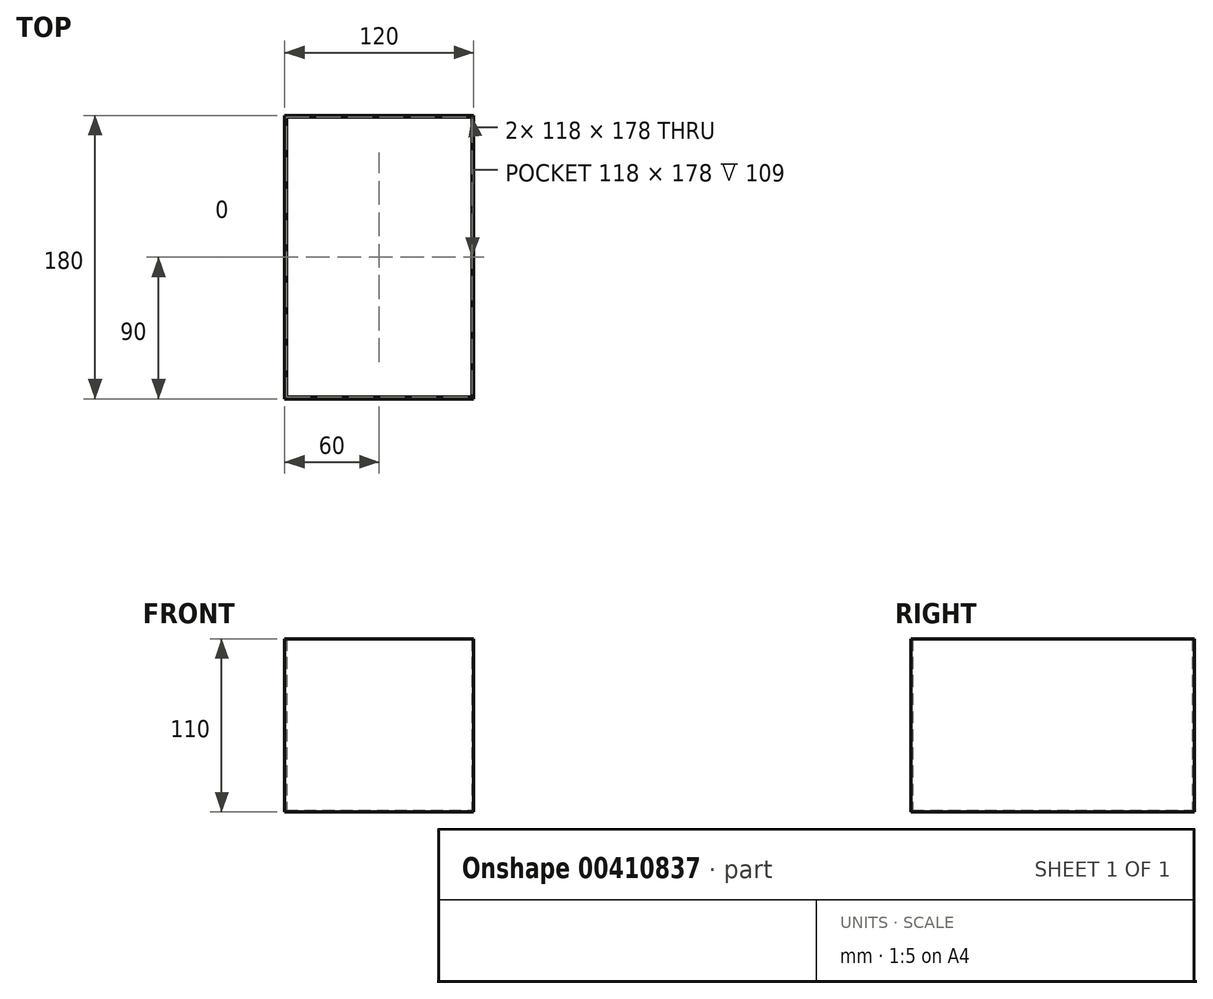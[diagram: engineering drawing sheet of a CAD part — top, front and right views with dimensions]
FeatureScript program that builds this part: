
annotation { "Feature Type Name" : "Feature", "Feature Type Description" : "" }
export const myFeature = defineFeature(function(context is Context, id is Id, definition is map)
    precondition{}
    {
        {
            var Q0;
            Q0=qCreatedBy(makeId("Top.planeOp"),FACE);
            var sketch = newSketch(context, id + "F0", { "sketchPlane" : qUnion([Q0])});
            skLineSegment(sketch, "E0.bottom", {"start": v(0, 0) * mm, "end": v(120, 0) * mm});
            skLineSegment(sketch, "E0.left", {"start": v(0, 0) * mm, "end": v(0, 180) * mm});
            skLineSegment(sketch, "E0.right", {"start": v(120, 0) * mm, "end": v(120, 180) * mm});
            skLineSegment(sketch, "E1", {"start": v(0, 180) * mm, "end": v(120, 180) * mm});
            skPoint(sketch, "E2.center.orphan", {"position": v(60, 180) * mm});
            skSolve(sketch);
        }
        {
            var Q0;
            Q0 = qSketchRegion(id + "F0", true);
            extrude(context, id + "F1", {"entities" : qUnion([Q0]), "depth" : 110 * mm});
        }
        {
            var Q0;
            Q0=makeQuery(id+"F1.opExtrude","CAP_FACE",FACE,{"disambiguationData":[OSD([sQuery(id+"F0.wireOp",EDGE,"E0.bottom"),sQuery(id+"F0.wireOp",EDGE,"E0.top"),sQuery(id+"F0.wireOp",EDGE,"E0.left"),sQuery(id+"F0.wireOp",EDGE,"E0.right")])],"isStart":false});
            shell(context, id + "F2", {"entities" : qUnion([Q0]), "thickness" : 1 * mm});
        }
    });
